# Revit family: CD64
name_source: partatom
category: Communication Devices
revit_build: Autodesk Revit 2014 (Build: 20140709_2115(x64)
units: mm (PartAtom-declared; Revit-internal decimal feet)

## types (1)
- Horn Loudspeaker
    100V Taps = 32.00 W
    70V Taps = 32.00 W
    Baffle Material = <By Category>
    Body Material = QF_Plastic - Black - Fine Textured
    Color = <By Category>
    Cost = 445.99 $
    Cost MSRP = 445.99 $
    Coverage Horizontal = 60.00°
    Coverage Vertical = 40.00°
    Depth = 14.98 "
    Description = PICTURE OF 60° X 40° CONSTANT DIRECTIVITY RE-ENTRANT PAGING HORN
    Dispersion Angle = 60.00°
    Enclosure Material = <By Category>
    Family Code (default) = LOUD SPEAKERS
    Grill Material = <By Category>
    Height = 18.25 "
    IQ Category = SPEAKERS
    Ingress Protection = IP-34
    Manufacturer = ATLAS SOUND
    Manufacturer URL = https://www.atlasied.com
    Market = Commercial, Higher Education, Emergency
    MasterFormat = 27 41 13
    MaterFormat Title = SPEAKERS
    Model = CD64
    Mount Material = QF_Plastic - Black - Fine Textured
    OmniClass Number = 23-37 17 13 19
    OmniClass Title = SPEAKERS
    Pitch = 0.00°
    Product Documentation Link = https://www.atlasied.com
    Product Page URL = https://www.atlasied.com
    Rotation = 0.00°
    SPL Max = 112
    ScheduleType |RF| = AtlasIED Master
    Speaker Dispersion = 60.00°
    Transformer Option = Yes
    URL = www.atlassound.com
    Vertical Symmetry = Yes
    Warranty = 5 Year
    Weight Product = 18.95
    Width = 22.76 "

## geometry (parser evidence)
native form markers: Blend x6, Sweep x3
no freeform markers — native parametric forms only
